# Revit family: Furniture-Lighted_Mirror_Cabinet-KOHLER-MaxiSpace-K-96106T_1
name_source: partatom
category: Lighting Fixtures
units: mm (PartAtom-declared; Revit-internal decimal feet)

## family parameters
Cut with Voids When Loaded = No
Host = Face
Light Source = Yes
OmniClass Number = 23.21.23.00
OmniClass Title = Residential Furniture and Equipment
Part Type = Normal
Room Calculation Point = No
Round Connector Dimension = Use Diameter
Shared = No

## types (2) — shared parameters
ADA Compliant = No
Apparent Load = 36 VA
Assembly Code = E2010
Color Filter = 16777215
Date Modified = 07/27/2022
Default Elevation = 60"
Description = Bona Mirror Cabinet 600mm
Dimming Lamp Color Temperature Shift = Incandescent Lamp Curve
Electrical Connector = Yes
Electrical Note = One Dedicated Circuit Required
Finish = Kohler-Metal-NA-Black
Hardware Included = No
Height = 30 1/2"
Lamp = LED
Length = 6"
Light Source Symbol Size = 2"
Manufacturer = Kohler Co.
Master Format 2014 = 41 53 13
Master Format 2014 Name = Storage Cabinets
Material = Aluminium
Model = K-96106T-L-NA
Product Documentation Link = https://files.kohler.com.cn
Product Name = MaxiSpace
Product Page URL = https://www.kohler.com.cn
URL = http://www.kohler.com.cn
Voltage = 220 V
WaterSense Certified = No
Wattage Comments = 36W
Width = 23 1/4"

## per-type parameters (varying)
| type | Emit from Line Length | Type |
| Left Door-NA-Black | 20" | 1 |
| Right Door-NA-Black | 15" | 2 |

## geometry (parser evidence)
native form markers: Sweep x5
no freeform markers — native parametric forms only
